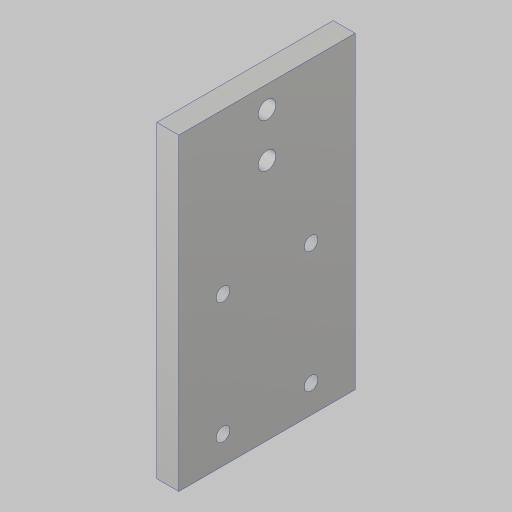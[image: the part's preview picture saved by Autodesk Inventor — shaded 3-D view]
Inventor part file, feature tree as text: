
AUTODESK INVENTOR PART (.ipt)
format: ipt  version: 2023.5 (Build 275446000, 446)  size: 113,664 bytes
history: native  units: in
note: dims shown in document units (in); Inventor stores cm internally (conversion verified against a paired STEP export)
features: sketch x2, hole x2, extrude x1
ambient origin geometry x8: Origin, YZ Plane, XZ Plane, XY Plane, X Axis, Y Axis, Z Axis, Center Point
bodies: Solid1 (feature_tree)
feature tree (5):
  extrude  "Extrusion1"  Depth=2.0in
  sketch  "Sketch2"  dims[d2=0.25in d3=0.0in d4=1.0in d5=1.375in d6=0.313in d7=0.5in d8=0.25in d9=0.156in d10=0.38in d11=0.507in d12=0.25in d13=0.5635in d14=1.0in d15=0.8108in d16=0.201in d17=0.38in d18=0.385in d19=0.25in d20=0.5635in d21=1.0in d22=0.8108in]
  hole  "Hole1"  [1 undecoded]
  hole  "Hole2"  [1 undecoded]
  sketch  "Sketch1"  dims[d0=3.5in d1=2.0in]
note: 2 required parameter values undecoded (feature->parameter linkage not recoverable at this tier; creation-order binding heuristic only, values carry confidence <= 0.55)
